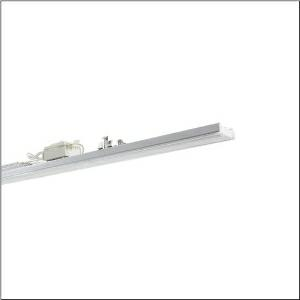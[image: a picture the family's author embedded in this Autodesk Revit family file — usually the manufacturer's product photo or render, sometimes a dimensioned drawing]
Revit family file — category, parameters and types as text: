
# Revit family: licross_r__21_recessed_mo_52te11cn49xg_3681
name_source: partatom
category: Lighting Fixtures
units: mm (PartAtom-declared; Revit-internal decimal feet)

## family parameters
Cut with Voids When Loaded = No
Host = Face
Light Source = No
Part Type = Normal
Room Calculation Point = No
Round Connector Dimension = Use Diameter
Shared = No

## types (1)
- --- (1 x LED, 9120 lm, 49.9 W, 4000K)
    Apparent Load = 50 VA
    CIE Flux Codes = 89 96 99 100 100
    Color Rendering = 80
    Color Temperature = 4000K
    Default Elevation = 1800 mm
    Description = Licross® 21 Recessed MO, luminaire insert, of sheet steel, galvanised, coil coated, white, length: 1.500mm, width: 66mm, height: 67mm, LED rated luminous flux: 9.120lm, light colour: 840, control gear: ON/OFF Multilumen, CLOi, control gear: ECG Multilumen, with plug, 3-pole, with phase selection, mains connection: 220..240V, AC, 50/60Hz, start of lifetime: 50W, end of service life: 61W, internal wiring halogen-free, primary light control with lens, of plastic, primary optical cover: cover, of PMMA, light emission: direct distribution, primary light characteristic: symmetric, protection rating (complete): IP54, insulation class (complete): insulation class I (protective earthing), certification: CE, ENEC, VDE, UKCA, protection symbol: D if used in an environment with non-conductive dust loads with corresponding accessories, impact resistance: IK06, permissible ambient temperature for indoor applications: -35..+40°C, corresponds to IFS (International Featured Standards) requirements for safety and quality in the food industry, reducing of maximum allowable ambient temperature of 5°C with ceiling mounting, LABS conformity tested according to VDMA 24364:2018-05, packaging unit: 1 piece
    Height = 58 mm
    Lamp = 1 x LED
    Lamp Light Flux = 9120 lm
    Lamp Power = 49.9 W
    Lamp count = 1
    Length = 1500 mm
    Luminous efficacy = 183 lm/W
    Manufacturer = Siteco
    ModVariant = No
    Model = 52TE11CN49XG
    Mounting Place = Ceiling
    Mounting Type = Pendant
    Number of Poles = 1
    OnlyDefault = Yes
    Power Factor = 1
    Product Name = Licross® 21 Recessed MO
    Product group = luminaire insert | ceiling pendant
    ProductGroupID = 902
    Protection Class = Protection class I
    Protection Degree = IP 54
    RLX_Detail_Level = 1
    RLX_Emergency_Light_Flux = 0 lm
    RLX_Emergency_Type = 0
    RLX_Emergency_Type_DB = No
    RlxData = <blob elided: 22281 chars, md5=a598380c>
    Socket = socket
    Standby Power = 0 W
    System Light Flux = 9120 lm
    System Power = 50 W
    Type Comments = factory setting: luminous flux: 100 % | (A | C | E) | 116 mA
    Type Image = l_1296930.jpg
    URL = http://relux.com
    VarID = @adj_132147
    Voltage = 0 V
    Weight = 0.00 kg
    Width = 66 mm

## geometry (parser evidence)
native form markers: Blend x4, Sweep x12
no freeform markers — native parametric forms only
